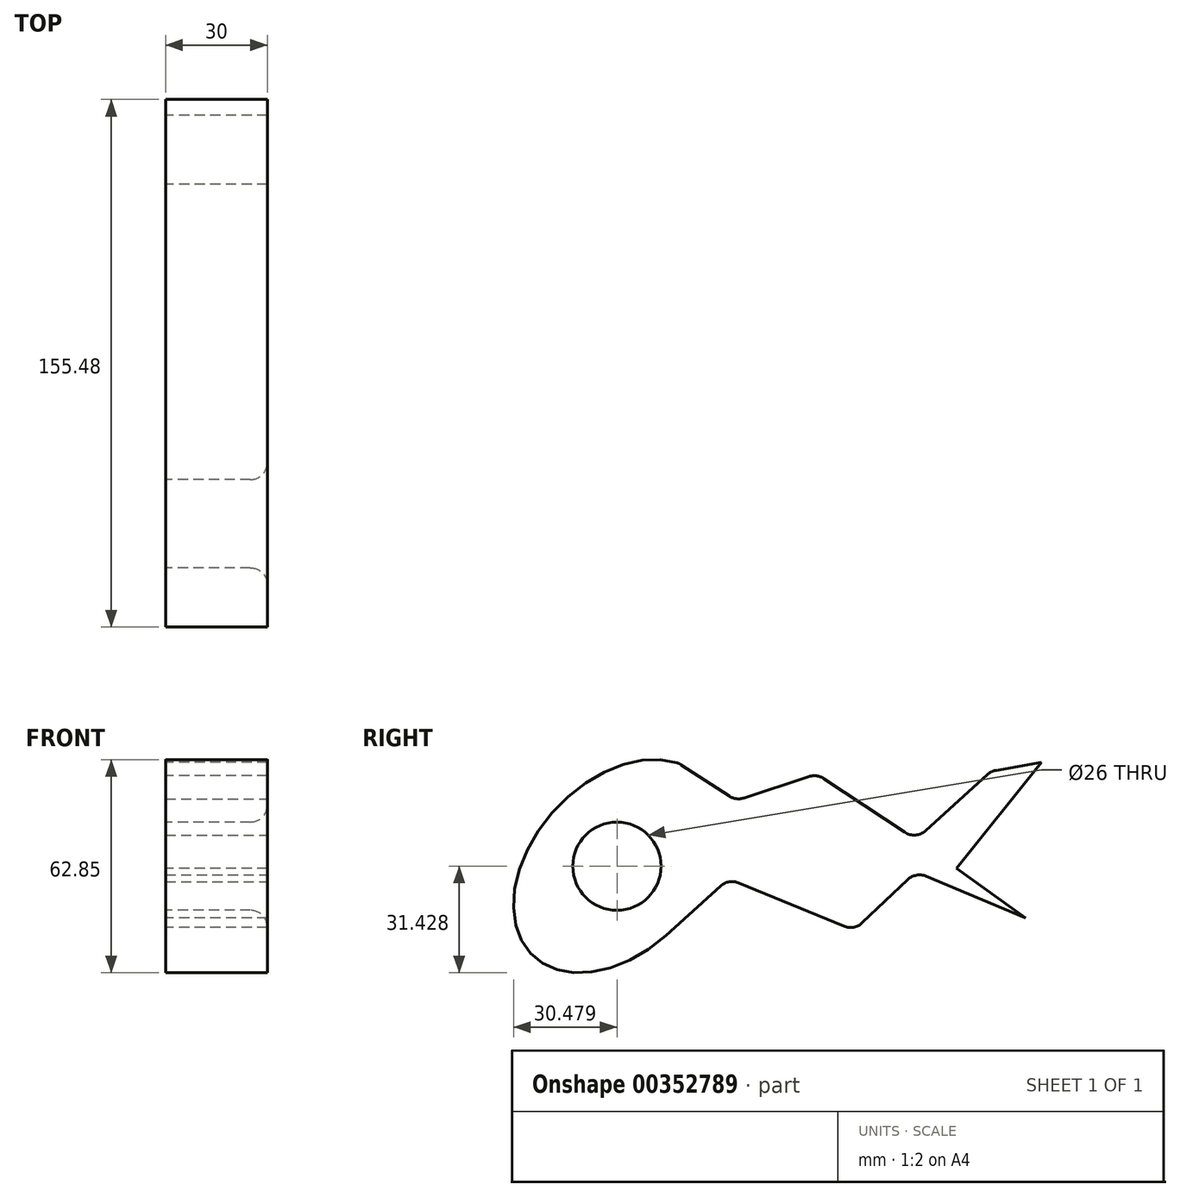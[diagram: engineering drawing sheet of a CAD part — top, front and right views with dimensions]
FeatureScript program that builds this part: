
annotation { "Feature Type Name" : "Feature", "Feature Type Description" : "" }
export const myFeature = defineFeature(function(context is Context, id is Id, definition is map)
    precondition{}
    {
        {
            var Q0;
            Q0=qCreatedBy(makeId("Right.planeOp"),FACE);
            var sketch = newSketch(context, id + "F0", { "sketchPlane" : qUnion([Q0])});
            skLineSegment(sketch, "E0", {"start": v(40.9, 30.9) * mm, "end": v(57.66, 19.99) * mm});
            skLineSegment(sketch, "E1", {"start": v(57.66, 19.99) * mm, "end": v(81.4, 27.8) * mm});
            skLineSegment(sketch, "E2", {"start": v(81.4, 27.8) * mm, "end": v(110.59, 8.48) * mm});
            skLineSegment(sketch, "E3", {"start": v(110.59, 8.48) * mm, "end": v(132.8, 28.65) * mm});
            skLineSegment(sketch, "E4", {"start": v(132.8, 28.65) * mm, "end": v(147.57, 31.22) * mm});
            skLineSegment(sketch, "E5", {"start": v(147.57, 31.22) * mm, "end": v(122.57, 0) * mm});
            skLineSegment(sketch, "E6", {"start": v(122.57, 0) * mm, "end": v(142.85, -14.62) * mm});
            skLineSegment(sketch, "E7", {"start": v(142.85, -14.62) * mm, "end": v(110.59, -1.05) * mm});
            skLineSegment(sketch, "E8", {"start": v(110.59, -1.05) * mm, "end": v(92.47, -18.27) * mm});
            skLineSegment(sketch, "E9", {"start": v(92.47, -18.27) * mm, "end": v(55.48, -3.05) * mm});
            skLineSegment(sketch, "E10", {"start": v(55.48, -3.05) * mm, "end": v(36.93, -19.8) * mm});
            skEllipticalArc(sketch, "E11", {});
            skCircle(sketch, "E12", {"center": v(22.57, 0.66) * mm, "radius": 13 * mm});
            const initialGuessF0  = {"E11": [0.022569214969499783, 0.000658193830022603, 0.6767807882511329, 0.7361845995768829, 0.03614845311678595, 0.024692923358508898, 0.28626338269580803, 4.563877103890591]};
            skSetInitialGuess(sketch, initialGuessF0);
            skSolve(sketch);
        }
        {
            var Q0;
            Q0=makeQuery(id+"F0.imprint","IMPRINT",FACE,{"disambiguationData":[TD([[makeQuery(id+"F0.imprint","IMPRINT",EDGE,{"derivedFrom":sQuery(id+"F0.wireOp",EDGE,"E0")}),-1.0]])]});
            extrude(context, id + "F1", {"entities" : qUnion([Q0]), "depth" : 30 * mm});
        }
        {
            var Q0;
            Q0=makeQuery(id+"F1.opExtrude","CAP_EDGE",EDGE,{"disambiguationData":[OSD([sQuery(id+"F0.wireOp",EDGE,"E12")])],"isStart":false});
            var Q1;
            Q1=makeQuery(id+"F1.opExtrude","SWEPT_EDGE",EDGE,{"disambiguationData":[OSD([sQuery(id+"F0.wireOp",EDGE,"E9"),sQuery(id+"F0.wireOp",EDGE,"E10")])]});
            var Q2;
            Q2=makeQuery(id+"F1.opExtrude","SWEPT_EDGE",EDGE,{"disambiguationData":[OSD([sQuery(id+"F0.wireOp",EDGE,"E8"),sQuery(id+"F0.wireOp",EDGE,"E9")])]});
            var Q3;
            Q3=makeQuery(id+"F1.opExtrude","SWEPT_EDGE",EDGE,{"disambiguationData":[OSD([sQuery(id+"F0.wireOp",EDGE,"E7"),sQuery(id+"F0.wireOp",EDGE,"E8")])]});
            var Q4;
            Q4=makeQuery(id+"F1.opExtrude","SWEPT_EDGE",EDGE,{"disambiguationData":[OSD([sQuery(id+"F0.wireOp",EDGE,"E3"),sQuery(id+"F0.wireOp",EDGE,"E4")])]});
            var Q5;
            Q5=makeQuery(id+"F1.opExtrude","SWEPT_EDGE",EDGE,{"disambiguationData":[OSD([sQuery(id+"F0.wireOp",EDGE,"E2"),sQuery(id+"F0.wireOp",EDGE,"E3")])]});
            var Q6;
            Q6=makeQuery(id+"F1.opExtrude","SWEPT_EDGE",EDGE,{"disambiguationData":[OSD([sQuery(id+"F0.wireOp",EDGE,"E1"),sQuery(id+"F0.wireOp",EDGE,"E2")])]});
            var Q7;
            Q7=makeQuery(id+"F1.opExtrude","SWEPT_EDGE",EDGE,{"disambiguationData":[OSD([sQuery(id+"F0.wireOp",EDGE,"E0"),sQuery(id+"F0.wireOp",EDGE,"E1")])]});
            var Q8;
            Q8=makeQuery(id+"F1.opExtrude","SWEPT_EDGE",EDGE,{"disambiguationData":[OSD([sQuery(id+"F0.wireOp",EDGE,"E0"),sQuery(id+"F0.wireOp",EDGE,"E11")])]});
            fillet(context, id + "F2", {"entities" : qUnion([Q0, Q1, Q2, Q3, Q4, Q5, Q6, Q7, Q8]), "radius" : 5 * mm, "tangentPropagation" : true, "allowEdgeOverflow" : false});
        }
    });
